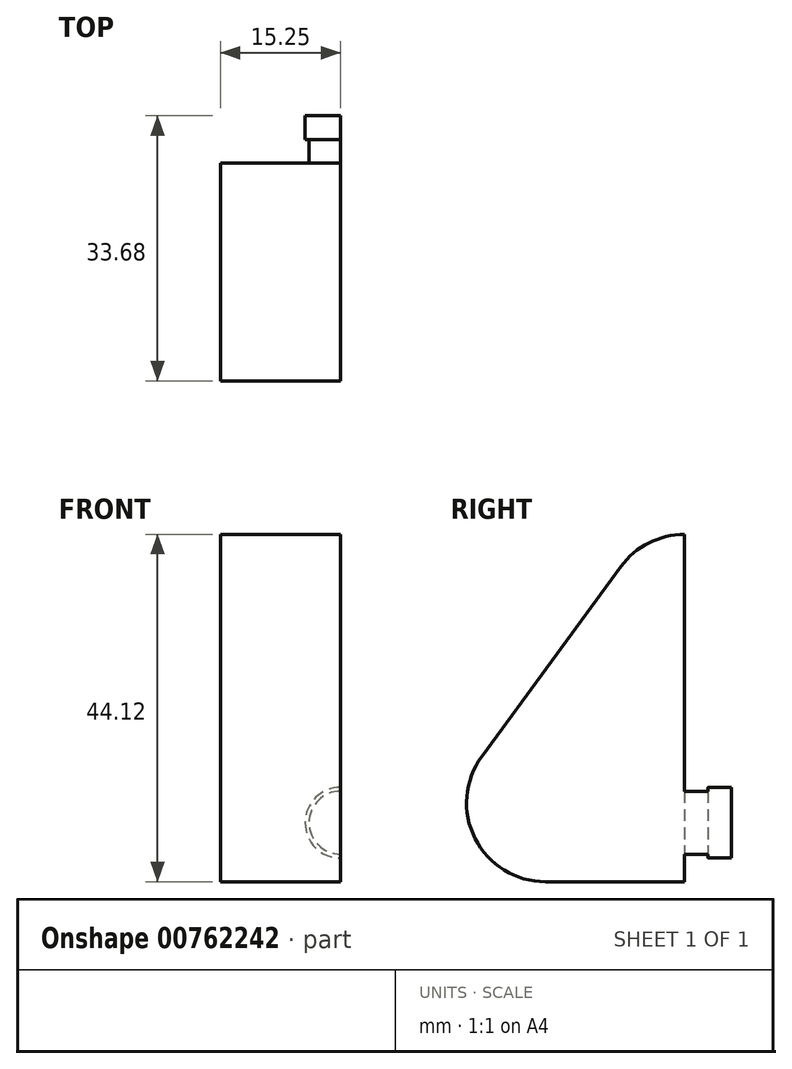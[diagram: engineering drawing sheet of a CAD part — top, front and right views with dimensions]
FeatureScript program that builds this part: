
annotation { "Feature Type Name" : "Feature", "Feature Type Description" : "" }
export const myFeature = defineFeature(function(context is Context, id is Id, definition is map)
    precondition{}
    {
        {
            var Q0;
            Q0=qCreatedBy(makeId("Right.planeOp"),FACE);
            var sketch = newSketch(context, id + "F0", { "sketchPlane" : qUnion([Q0])});
            skLineSegment(sketch, "E0.bottom", {"start": v(27.36, 43.18) * mm, "end": v(-7.64, 43.18) * mm});
            skLineSegment(sketch, "E0.top", {"start": v(27.36, -0.94) * mm, "end": v(-7.64, -0.94) * mm});
            skLineSegment(sketch, "E0.left", {"start": v(27.36, 43.18) * mm, "end": v(27.36, -0.94) * mm});
            skLineSegment(sketch, "E0.right", {"start": v(-7.64, 43.18) * mm, "end": v(-7.64, -0.94) * mm});
            skCircle(sketch, "E1", {"center": v(27.36, 33.18) * mm, "radius": 10 * mm});
            skCircle(sketch, "E2", {"center": v(2.36, -0.94) * mm, "radius": 10 * mm});
            skLineSegment(sketch, "E3", {"start": v(27.36, 33.18) * mm, "end": v(2.36, -0.94) * mm});
            skLineSegment(sketch, "E4", {"start": v(2.36, -0.94) * mm, "end": v(-5.7, 4.97) * mm});
            skLineSegment(sketch, "E5", {"start": v(27.36, 33.18) * mm, "end": v(19.3, 39.1) * mm});
            skLineSegment(sketch, "E6", {"start": v(19.3, 39.1) * mm, "end": v(-5.7, 4.97) * mm});
            skSolve(sketch);
        }
        {
            var Q0;
            {var subQ3=sQuery(id+"F0.wireOp",EDGE,"E5");Q0=makeQuery(id+"F0.imprint","IMPRINT",FACE,{"disambiguationData":[TD([[makeQuery(id+"F0.imprint","IMPRINT",EDGE,{"derivedFrom":subQ3}),-1.0]])]});}
            var Q1;
            {var subQ0=sQuery(id+"F0.wireOp",EDGE,"E5");Q1=makeQuery(id+"F0.imprint","IMPRINT",FACE,{"disambiguationData":[TD([[makeQuery(id+"F0.imprint","IMPRINT",EDGE,{"derivedFrom":subQ0}),1.0]])]});}
            var Q2;
            {var subQ1=sQuery(id+"F0.wireOp",EDGE,"E0.left");var subQ3=sQuery(id+"F0.wireOp",EDGE,"E1");var subQ4=makeQuery(id+"F0.imprint","INTERSECT",VERTEX,{"derivedFrom":[subQ1,subQ3]});Q2=makeQuery(id+"F0.imprint","IMPRINT",FACE,{"disambiguationData":[TD([[makeQuery(id+"F0.imprint","IMPRINT",EDGE,{"disambiguationData":[TD([[subQ4,1.0]])],"derivedFrom":subQ3}),1.0]])]});}
            var Q3;
            {var subQ1=sQuery(id+"F0.wireOp",EDGE,"E0.top");var subQ5=sQuery(id+"F0.wireOp",EDGE,"E0.left");var subQ6=makeQuery(id+"F0.imprint","INTERSECT",VERTEX,{"derivedFrom":[subQ1,subQ5]});Q3=makeQuery(id+"F0.imprint","IMPRINT",FACE,{"disambiguationData":[TD([[makeQuery(id+"F0.imprint","IMPRINT",EDGE,{"disambiguationData":[TD([[subQ6,-1.0]])],"derivedFrom":subQ1}),-1.0]])]});}
            var Q4;
            {var subQ0=sQuery(id+"F0.wireOp",EDGE,"E6");Q4=makeQuery(id+"F0.imprint","IMPRINT",FACE,{"disambiguationData":[TD([[makeQuery(id+"F0.imprint","IMPRINT",EDGE,{"derivedFrom":subQ0}),1.0]])]});}
            var Q5;
            {var subQ0=sQuery(id+"F0.wireOp",EDGE,"E4");Q5=makeQuery(id+"F0.imprint","IMPRINT",FACE,{"disambiguationData":[TD([[makeQuery(id+"F0.imprint","IMPRINT",EDGE,{"derivedFrom":subQ0}),-1.0]])]});}
            var Q6;
            {var subQ3=sQuery(id+"F0.wireOp",EDGE,"E4");Q6=makeQuery(id+"F0.imprint","IMPRINT",FACE,{"disambiguationData":[TD([[makeQuery(id+"F0.imprint","IMPRINT",EDGE,{"derivedFrom":subQ3}),1.0]])]});}
            var Q7;
            {var subQ1=sQuery(id+"F0.wireOp",EDGE,"E0.top");var subQ3=sQuery(id+"F0.wireOp",EDGE,"E2");var subQ4=makeQuery(id+"F0.imprint","INTERSECT",VERTEX,{"derivedFrom":[subQ1,subQ3]});Q7=makeQuery(id+"F0.imprint","IMPRINT",FACE,{"disambiguationData":[TD([[makeQuery(id+"F0.imprint","IMPRINT",EDGE,{"disambiguationData":[TD([[subQ4,-1.0]])],"derivedFrom":subQ3}),1.0]])]});}
            extrude(context, id + "F1", {"entities" : qUnion([Q0, Q1, Q2, Q3, Q4, Q5, Q6, Q7]), "depth" : (13 + 17.5) / 2 * mm, "offsetDistance" : 25 * mm});
        }
        {
            var Q0;
            Q0=makeQuery(id+"F1.opExtrude","SWEPT_EDGE",EDGE,{"disambiguationData":[OSD([sQuery(id+"F0.wireOp",EDGE,"E0.top"),sQuery(id+"F0.wireOp",EDGE,"E0.right"),sQuery(id+"F0.wireOp",EDGE,"E2")])]});
            fillet(context, id + "F2", {"entities" : qUnion([Q0]), "radius" : 10 * mm, "tangentPropagation" : true, "allowEdgeOverflow" : false});
        }
        {
            var Q0;
            Q0=makeQuery(id+"F1.opExtrude","CAP_FACE",FACE,{"disambiguationData":[OSD([sQuery(id+"F0.wireOp",EDGE,"E0.top"),sQuery(id+"F0.wireOp",EDGE,"E0.left"),sQuery(id+"F0.wireOp",EDGE,"E1"),sQuery(id+"F0.wireOp",EDGE,"E2"),sQuery(id+"F0.wireOp",EDGE,"E6")])],"isStart":false});
            var sketch = newSketch(context, id + "F3", { "sketchPlane" : qUnion([Q0])});
            skLineSegment(sketch, "E7.bottom", {"start": v(27.36, 6.56) * mm, "end": v(30.36, 6.56) * mm});
            skLineSegment(sketch, "E7.top", {"start": v(27.36, 2.56) * mm, "end": v(30.36, 2.56) * mm});
            skLineSegment(sketch, "E7.left", {"start": v(27.36, 6.56) * mm, "end": v(27.36, 2.56) * mm});
            skLineSegment(sketch, "E7.right", {"start": v(30.36, 6.56) * mm, "end": v(30.36, 2.56) * mm});
            skLineSegment(sketch, "E8.bottom", {"start": v(30.36, 6.56) * mm, "end": v(33.36, 6.56) * mm});
            skLineSegment(sketch, "E8.top", {"start": v(30.36, 2.06) * mm, "end": v(33.36, 2.06) * mm});
            skLineSegment(sketch, "E8.left", {"start": v(30.36, 6.56) * mm, "end": v(30.36, 2.06) * mm});
            skLineSegment(sketch, "E8.right", {"start": v(33.36, 6.56) * mm, "end": v(33.36, 2.06) * mm});
            skSolve(sketch);
        }
        {
            var Q0;
            {var subQ0=sQuery(id+"F3.wireOp",EDGE,"E7.bottom");Q0=makeQuery(id+"F3.imprint","IMPRINT",FACE,{"disambiguationData":[TD([[makeQuery(id+"F3.imprint","IMPRINT",EDGE,{"derivedFrom":subQ0}),-1.0]])]});}
            var Q1;
            {var subQ3=sQuery(id+"F3.wireOp",EDGE,"E8.bottom");Q1=makeQuery(id+"F3.imprint","IMPRINT",FACE,{"disambiguationData":[TD([[makeQuery(id+"F3.imprint","IMPRINT",EDGE,{"derivedFrom":subQ3}),-1.0]])]});}
            var Q2;
            Q2=sQuery(id+"F3.wireOp",EDGE,"E7.bottom");
            revolve(context, id + "F4", {"operationType" : NewBodyOperationType.ADD, "surfaceOperationType" : NewSurfaceOperationType.NEW, "entities" : qUnion([Q0, Q1]), "axis" : qUnion([Q2]), "revolveType" : RevolveType.ONE_DIRECTION, "angle" : 180 * degree});
        }
    });
